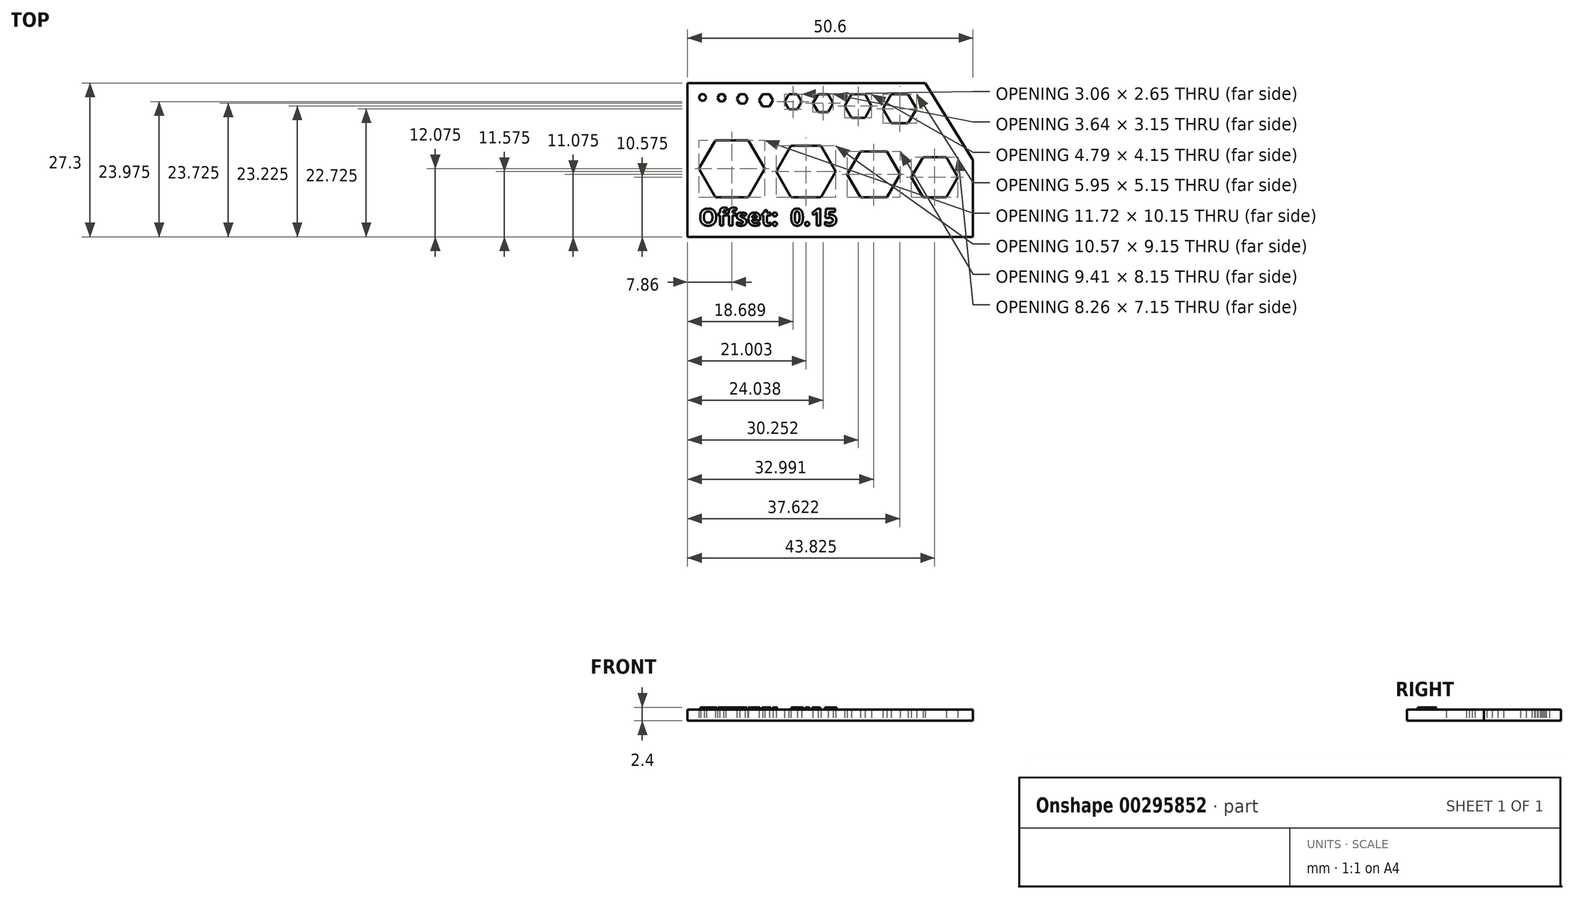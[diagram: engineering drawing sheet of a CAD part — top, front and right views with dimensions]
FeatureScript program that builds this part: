
annotation { "Feature Type Name" : "Feature", "Feature Type Description" : "" }
export const myFeature = defineFeature(function(context is Context, id is Id, definition is map)
    precondition{}
    {
        {
            assignVariable(context, id + "F0", {"variableType" : VariableType.LENGTH, "name" : "HoleOffset", "lengthValue" : 0.15 * mm});
        }
        {
            assignVariable(context, id + "F1", {"variableType" : VariableType.LENGTH, "name" : "HoleDistance", "lengthValue" : 2 * mm});
        }
        {
            assignVariable(context, id + "F2", {"variableType" : VariableType.LENGTH, "name" : "TextHeight", "lengthValue" : 3 * mm});
        }
        {
            assignVariable(context, id + "F3", {"variableType" : VariableType.LENGTH, "name" : "TextRelief", "lengthValue" : 0.4 * mm});
        }
        {
            assignVariable(context, id + "F4", {"variableType" : VariableType.LENGTH, "name" : "BaseWidth", "lengthValue" : 40 * mm + getVariable(context, 'HoleDistance') * 5 + getVariable(context, 'HoleOffset') * 4});
        }
        {
            assignVariable(context, id + "F5", {"variableType" : VariableType.LENGTH, "name" : "BaseHeight", "lengthValue" : 16 * mm + getVariable(context, 'TextHeight') + getVariable(context, 'HoleDistance') * 4 + getVariable(context, 'HoleOffset') * 2});
        }
        {
            assignVariable(context, id + "F6", {"variableType" : VariableType.LENGTH, "name" : "BaseThickness", "lengthValue" : 2 * mm});
        }
        {
            var Q0;
            Q0=qCreatedBy(makeId("Top.planeOp"),FACE);
            var sketch = newSketch(context, id + "F7", { "sketchPlane" : qUnion([Q0])});
            skLineSegment(sketch, "E0.bottom", {"start": v(0, 0) * mm, "end": v(50.6, 0) * mm});
            skLineSegment(sketch, "E0.top", {"start": v(0, -27.3) * mm, "end": v(50.6, -27.3) * mm});
            skLineSegment(sketch, "E0.left", {"start": v(0, 0) * mm, "end": v(0, -27.3) * mm});
            skLineSegment(sketch, "E0.right", {"start": v(50.6, 0) * mm, "end": v(50.6, -27.3) * mm});
            skCircle(sketch, "E1.cCircle", {"center": v(2.66, -2.57) * mm, "radius": 0.57 * mm, "construction": true});
            skLineSegment(sketch, "E1.0", {"start": v(3.33, -2.58) * mm, "end": v(3, -3.15) * mm});
            skLineSegment(sketch, "E1.1", {"start": v(3, -3.15) * mm, "end": v(2.33, -3.15) * mm});
            skLineSegment(sketch, "E1.2", {"start": v(2.33, -3.15) * mm, "end": v(2, -2.57) * mm});
            skLineSegment(sketch, "E1.3", {"start": v(2, -2.57) * mm, "end": v(2.33, -2) * mm});
            skLineSegment(sketch, "E1.4", {"start": v(2.33, -2) * mm, "end": v(3, -2) * mm});
            skLineSegment(sketch, "E1.5", {"start": v(3, -2) * mm, "end": v(3.33, -2.57) * mm});
            skPoint(sketch, "E1.0.midPoint", {"position": v(3.16, -2.86) * mm});
            skCircle(sketch, "E2.cCircle", {"center": v(6.05, -2.62) * mm, "radius": 0.62 * mm, "construction": true});
            skLineSegment(sketch, "E2.0", {"start": v(6.77, -2.63) * mm, "end": v(6.41, -3.25) * mm});
            skLineSegment(sketch, "E2.1", {"start": v(6.41, -3.25) * mm, "end": v(5.69, -3.25) * mm});
            skLineSegment(sketch, "E2.2", {"start": v(5.69, -3.25) * mm, "end": v(5.33, -2.62) * mm});
            skLineSegment(sketch, "E2.3", {"start": v(5.33, -2.62) * mm, "end": v(5.69, -2) * mm});
            skLineSegment(sketch, "E2.4", {"start": v(5.69, -2) * mm, "end": v(6.41, -2) * mm});
            skLineSegment(sketch, "E2.5", {"start": v(6.41, -2) * mm, "end": v(6.77, -2.62) * mm});
            skPoint(sketch, "E2.0.midPoint", {"position": v(6.6, -2.94) * mm});
            skCircle(sketch, "E3.cCircle", {"center": v(9.72, -2.82) * mm, "radius": 0.82 * mm, "construction": true});
            skLineSegment(sketch, "E3.0", {"start": v(10.68, -2.83) * mm, "end": v(10.2, -3.65) * mm});
            skLineSegment(sketch, "E3.1", {"start": v(10.2, -3.65) * mm, "end": v(9.25, -3.65) * mm});
            skLineSegment(sketch, "E3.2", {"start": v(9.25, -3.65) * mm, "end": v(8.77, -2.82) * mm});
            skLineSegment(sketch, "E3.3", {"start": v(8.77, -2.82) * mm, "end": v(9.25, -2) * mm});
            skLineSegment(sketch, "E3.4", {"start": v(9.25, -2) * mm, "end": v(10.2, -2) * mm});
            skLineSegment(sketch, "E3.5", {"start": v(10.2, -2) * mm, "end": v(10.68, -2.83) * mm});
            skPoint(sketch, "E3.0.midPoint", {"position": v(10.44, -3.24) * mm});
            skCircle(sketch, "E4.cCircle", {"center": v(13.92, -3.07) * mm, "radius": 1.07 * mm, "construction": true});
            skLineSegment(sketch, "E4.0", {"start": v(15.16, -3.07) * mm, "end": v(14.54, -4.15) * mm});
            skLineSegment(sketch, "E4.1", {"start": v(14.54, -4.15) * mm, "end": v(13.3, -4.15) * mm});
            skLineSegment(sketch, "E4.2", {"start": v(13.3, -4.15) * mm, "end": v(12.68, -3.07) * mm});
            skLineSegment(sketch, "E4.3", {"start": v(12.68, -3.07) * mm, "end": v(13.3, -2) * mm});
            skLineSegment(sketch, "E4.4", {"start": v(13.3, -2) * mm, "end": v(14.54, -2) * mm});
            skLineSegment(sketch, "E4.5", {"start": v(14.54, -2) * mm, "end": v(15.16, -3.07) * mm});
            skPoint(sketch, "E4.0.midPoint", {"position": v(14.85, -3.61) * mm});
            skCircle(sketch, "E5.cCircle", {"center": v(18.69, -3.32) * mm, "radius": 1.32 * mm, "construction": true});
            skLineSegment(sketch, "E5.0", {"start": v(20.22, -3.33) * mm, "end": v(19.45, -4.65) * mm});
            skLineSegment(sketch, "E5.1", {"start": v(19.45, -4.65) * mm, "end": v(17.92, -4.65) * mm});
            skLineSegment(sketch, "E5.2", {"start": v(17.92, -4.65) * mm, "end": v(17.16, -3.32) * mm});
            skLineSegment(sketch, "E5.3", {"start": v(17.16, -3.32) * mm, "end": v(17.92, -2) * mm});
            skLineSegment(sketch, "E5.4", {"start": v(17.92, -2) * mm, "end": v(19.45, -2) * mm});
            skLineSegment(sketch, "E5.5", {"start": v(19.45, -2) * mm, "end": v(20.22, -3.33) * mm});
            skPoint(sketch, "E5.0.midPoint", {"position": v(19.84, -3.99) * mm});
            skCircle(sketch, "E6.cCircle", {"center": v(24.04, -3.57) * mm, "radius": 1.57 * mm, "construction": true});
            skLineSegment(sketch, "E6.0", {"start": v(25.86, -3.58) * mm, "end": v(24.95, -5.15) * mm});
            skLineSegment(sketch, "E6.1", {"start": v(24.95, -5.15) * mm, "end": v(23.13, -5.15) * mm});
            skLineSegment(sketch, "E6.2", {"start": v(23.13, -5.15) * mm, "end": v(22.22, -3.58) * mm});
            skLineSegment(sketch, "E6.3", {"start": v(22.22, -3.58) * mm, "end": v(23.13, -2) * mm});
            skLineSegment(sketch, "E6.4", {"start": v(23.13, -2) * mm, "end": v(24.95, -2) * mm});
            skLineSegment(sketch, "E6.5", {"start": v(24.95, -2) * mm, "end": v(25.86, -3.57) * mm});
            skPoint(sketch, "E6.0.midPoint", {"position": v(25.4, -4.36) * mm});
            skCircle(sketch, "E7.cCircle", {"center": v(30.25, -4.08) * mm, "radius": 2.08 * mm, "construction": true});
            skLineSegment(sketch, "E7.0", {"start": v(32.65, -4.07) * mm, "end": v(31.45, -6.15) * mm});
            skLineSegment(sketch, "E7.1", {"start": v(31.45, -6.15) * mm, "end": v(29.05, -6.15) * mm});
            skLineSegment(sketch, "E7.2", {"start": v(29.05, -6.15) * mm, "end": v(27.86, -4.08) * mm});
            skLineSegment(sketch, "E7.3", {"start": v(27.86, -4.08) * mm, "end": v(29.05, -2) * mm});
            skLineSegment(sketch, "E7.4", {"start": v(29.05, -2) * mm, "end": v(31.45, -2) * mm});
            skLineSegment(sketch, "E7.5", {"start": v(31.45, -2) * mm, "end": v(32.65, -4.07) * mm});
            skPoint(sketch, "E7.0.midPoint", {"position": v(32.05, -5.11) * mm});
            skCircle(sketch, "E8.cCircle", {"center": v(37.62, -4.58) * mm, "radius": 2.58 * mm, "construction": true});
            skLineSegment(sketch, "E8.0", {"start": v(40.6, -4.58) * mm, "end": v(39.1, -7.15) * mm});
            skLineSegment(sketch, "E8.1", {"start": v(39.1, -7.15) * mm, "end": v(36.14, -7.15) * mm});
            skLineSegment(sketch, "E8.2", {"start": v(36.14, -7.15) * mm, "end": v(34.65, -4.57) * mm});
            skLineSegment(sketch, "E8.3", {"start": v(34.65, -4.58) * mm, "end": v(36.14, -2) * mm});
            skLineSegment(sketch, "E8.4", {"start": v(36.14, -2) * mm, "end": v(39.1, -2) * mm});
            skLineSegment(sketch, "E8.5", {"start": v(39.1, -2) * mm, "end": v(40.6, -4.57) * mm});
            skPoint(sketch, "E8.0.midPoint", {"position": v(39.85, -5.86) * mm});
            skCircle(sketch, "E9.cCircle", {"center": v(7.86, -15.23) * mm, "radius": 5.08 * mm, "construction": true});
            skLineSegment(sketch, "E9.0", {"start": v(13.72, -15.23) * mm, "end": v(10.8, -20.3) * mm});
            skLineSegment(sketch, "E9.1", {"start": v(10.8, -20.3) * mm, "end": v(4.93, -20.3) * mm});
            skLineSegment(sketch, "E9.2", {"start": v(4.93, -20.3) * mm, "end": v(2, -15.23) * mm});
            skLineSegment(sketch, "E9.3", {"start": v(2, -15.22) * mm, "end": v(4.93, -10.15) * mm});
            skLineSegment(sketch, "E9.4", {"start": v(4.93, -10.15) * mm, "end": v(10.8, -10.15) * mm});
            skLineSegment(sketch, "E9.5", {"start": v(10.8, -10.15) * mm, "end": v(13.72, -15.23) * mm});
            skPoint(sketch, "E9.0.midPoint", {"position": v(12.26, -17.76) * mm});
            skCircle(sketch, "E10.cCircle", {"center": v(21, -15.72) * mm, "radius": 4.58 * mm, "construction": true});
            skLineSegment(sketch, "E10.0", {"start": v(26.29, -15.72) * mm, "end": v(23.64, -20.3) * mm});
            skLineSegment(sketch, "E10.1", {"start": v(23.64, -20.3) * mm, "end": v(18.36, -20.3) * mm});
            skLineSegment(sketch, "E10.2", {"start": v(18.36, -20.3) * mm, "end": v(15.72, -15.72) * mm});
            skLineSegment(sketch, "E10.3", {"start": v(15.72, -15.73) * mm, "end": v(18.36, -11.15) * mm});
            skLineSegment(sketch, "E10.4", {"start": v(18.36, -11.15) * mm, "end": v(23.64, -11.15) * mm});
            skLineSegment(sketch, "E10.5", {"start": v(23.64, -11.15) * mm, "end": v(26.29, -15.72) * mm});
            skPoint(sketch, "E10.0.midPoint", {"position": v(24.97, -18.01) * mm});
            skCircle(sketch, "E11.cCircle", {"center": v(33, -16.23) * mm, "radius": 4.08 * mm, "construction": true});
            skLineSegment(sketch, "E11.0", {"start": v(37.7, -16.23) * mm, "end": v(35.34, -20.3) * mm});
            skLineSegment(sketch, "E11.1", {"start": v(35.34, -20.3) * mm, "end": v(30.64, -20.3) * mm});
            skLineSegment(sketch, "E11.2", {"start": v(30.64, -20.3) * mm, "end": v(28.29, -16.22) * mm});
            skLineSegment(sketch, "E11.3", {"start": v(28.29, -16.22) * mm, "end": v(30.64, -12.15) * mm});
            skLineSegment(sketch, "E11.4", {"start": v(30.64, -12.15) * mm, "end": v(35.34, -12.15) * mm});
            skLineSegment(sketch, "E11.5", {"start": v(35.34, -12.15) * mm, "end": v(37.7, -16.23) * mm});
            skPoint(sketch, "E11.0.midPoint", {"position": v(36.52, -18.26) * mm});
            skCircle(sketch, "E12.cCircle", {"center": v(43.82, -16.72) * mm, "radius": 3.58 * mm, "construction": true});
            skLineSegment(sketch, "E12.0", {"start": v(47.95, -16.73) * mm, "end": v(45.89, -20.3) * mm});
            skLineSegment(sketch, "E12.1", {"start": v(45.89, -20.3) * mm, "end": v(41.76, -20.3) * mm});
            skLineSegment(sketch, "E12.2", {"start": v(41.76, -20.3) * mm, "end": v(39.7, -16.72) * mm});
            skLineSegment(sketch, "E12.3", {"start": v(39.7, -16.72) * mm, "end": v(41.76, -13.15) * mm});
            skLineSegment(sketch, "E12.4", {"start": v(41.76, -13.15) * mm, "end": v(45.89, -13.15) * mm});
            skLineSegment(sketch, "E12.5", {"start": v(45.89, -13.15) * mm, "end": v(47.95, -16.72) * mm});
            skPoint(sketch, "E12.0.midPoint", {"position": v(46.92, -18.51) * mm});
            skSolve(sketch);
        }
        {
            var Q0;
            Q0=makeQuery(id+"F7.imprint","IMPRINT",FACE,{"disambiguationData":[TD([[makeQuery(id+"F7.imprint","IMPRINT",EDGE,{"derivedFrom":sQuery(id+"F7.wireOp",EDGE,"E0.bottom")}),-1.0]])]});
            extrude(context, id + "F8", {"entities" : qUnion([Q0]), "depth" : getVariable(context, 'BaseThickness'), "offsetDistance" : 25 * mm});
        }
        {
            var Q0;
            Q0=makeQuery(id+"F8.opExtrude","CAP_FACE",FACE,{"disambiguationData":[OSD([sQuery(id+"F7.wireOp",EDGE,"E0.bottom"),sQuery(id+"F7.wireOp",EDGE,"E0.top"),sQuery(id+"F7.wireOp",EDGE,"E0.left"),sQuery(id+"F7.wireOp",EDGE,"E0.right"),sQuery(id+"F7.wireOp",EDGE,"E1.0"),sQuery(id+"F7.wireOp",EDGE,"E1.1"),sQuery(id+"F7.wireOp",EDGE,"E1.2"),sQuery(id+"F7.wireOp",EDGE,"E1.3"),sQuery(id+"F7.wireOp",EDGE,"E1.4"),sQuery(id+"F7.wireOp",EDGE,"E1.5"),sQuery(id+"F7.wireOp",EDGE,"E2.0"),sQuery(id+"F7.wireOp",EDGE,"E2.1"),sQuery(id+"F7.wireOp",EDGE,"E2.2"),sQuery(id+"F7.wireOp",EDGE,"E2.3"),sQuery(id+"F7.wireOp",EDGE,"E2.4"),sQuery(id+"F7.wireOp",EDGE,"E2.5"),sQuery(id+"F7.wireOp",EDGE,"E3.0"),sQuery(id+"F7.wireOp",EDGE,"E3.1"),sQuery(id+"F7.wireOp",EDGE,"E3.2"),sQuery(id+"F7.wireOp",EDGE,"E3.3"),sQuery(id+"F7.wireOp",EDGE,"E3.4"),sQuery(id+"F7.wireOp",EDGE,"E3.5"),sQuery(id+"F7.wireOp",EDGE,"E4.0"),sQuery(id+"F7.wireOp",EDGE,"E4.1"),sQuery(id+"F7.wireOp",EDGE,"E4.2"),sQuery(id+"F7.wireOp",EDGE,"E4.3"),sQuery(id+"F7.wireOp",EDGE,"E4.4"),sQuery(id+"F7.wireOp",EDGE,"E4.5"),sQuery(id+"F7.wireOp",EDGE,"E5.0"),sQuery(id+"F7.wireOp",EDGE,"E5.1"),sQuery(id+"F7.wireOp",EDGE,"E5.2"),sQuery(id+"F7.wireOp",EDGE,"E5.3"),sQuery(id+"F7.wireOp",EDGE,"E5.4"),sQuery(id+"F7.wireOp",EDGE,"E5.5"),sQuery(id+"F7.wireOp",EDGE,"E6.0"),sQuery(id+"F7.wireOp",EDGE,"E6.1"),sQuery(id+"F7.wireOp",EDGE,"E6.2"),sQuery(id+"F7.wireOp",EDGE,"E6.3"),sQuery(id+"F7.wireOp",EDGE,"E6.4"),sQuery(id+"F7.wireOp",EDGE,"E6.5"),sQuery(id+"F7.wireOp",EDGE,"E7.0"),sQuery(id+"F7.wireOp",EDGE,"E7.1"),sQuery(id+"F7.wireOp",EDGE,"E7.2"),sQuery(id+"F7.wireOp",EDGE,"E7.3"),sQuery(id+"F7.wireOp",EDGE,"E7.4"),sQuery(id+"F7.wireOp",EDGE,"E7.5"),sQuery(id+"F7.wireOp",EDGE,"E8.0"),sQuery(id+"F7.wireOp",EDGE,"E8.1"),sQuery(id+"F7.wireOp",EDGE,"E8.2"),sQuery(id+"F7.wireOp",EDGE,"E8.3"),sQuery(id+"F7.wireOp",EDGE,"E8.4"),sQuery(id+"F7.wireOp",EDGE,"E8.5"),sQuery(id+"F7.wireOp",EDGE,"E9.0"),sQuery(id+"F7.wireOp",EDGE,"E9.1"),sQuery(id+"F7.wireOp",EDGE,"E9.2"),sQuery(id+"F7.wireOp",EDGE,"E9.3"),sQuery(id+"F7.wireOp",EDGE,"E9.4"),sQuery(id+"F7.wireOp",EDGE,"E9.5"),sQuery(id+"F7.wireOp",EDGE,"E10.0"),sQuery(id+"F7.wireOp",EDGE,"E10.1"),sQuery(id+"F7.wireOp",EDGE,"E10.2"),sQuery(id+"F7.wireOp",EDGE,"E10.3"),sQuery(id+"F7.wireOp",EDGE,"E10.4"),sQuery(id+"F7.wireOp",EDGE,"E10.5"),sQuery(id+"F7.wireOp",EDGE,"E11.0"),sQuery(id+"F7.wireOp",EDGE,"E11.1"),sQuery(id+"F7.wireOp",EDGE,"E11.2"),sQuery(id+"F7.wireOp",EDGE,"E11.3"),sQuery(id+"F7.wireOp",EDGE,"E11.4"),sQuery(id+"F7.wireOp",EDGE,"E11.5"),sQuery(id+"F7.wireOp",EDGE,"E12.0"),sQuery(id+"F7.wireOp",EDGE,"E12.1"),sQuery(id+"F7.wireOp",EDGE,"E12.2"),sQuery(id+"F7.wireOp",EDGE,"E12.3"),sQuery(id+"F7.wireOp",EDGE,"E12.4"),sQuery(id+"F7.wireOp",EDGE,"E12.5")])],"isStart":false});
            cPlane(context, id + "F9", {"entities" : qUnion([Q0]), "cplaneType" : CPlaneType.OFFSET, "offset" : 0 * mm, "width" : 150 * mm, "height" : 150 * mm});
        }
        {
            var Q0;
            Q0=qCreatedBy(id+"F9.planeOp",FACE);
            var sketch = newSketch(context, id + "F10", { "sketchPlane" : qUnion([Q0])});
            skText(sketch, "E13", { "text": "Offset:  0.15", "fontName": "OpenSans-Bold.ttf"});
            const initialGuessF10  = {"E13": [0.002, -0.0253, 1, 0, 0.003]};
            skSetInitialGuess(sketch, initialGuessF10);
            skSolve(sketch);
        }
        {
            var Q0;
            Q0 = qSketchRegion(id + "F10", true);
            extrude(context, id + "F11", {"entities" : qUnion([Q0]), "operationType" : NewBodyOperationType.ADD, "depth" : getVariable(context, 'TextRelief'), "offsetDistance" : 25 * mm});
        }
        {
            var Q0;
            Q0=makeQuery(id+"F8.opExtrude","SWEPT_EDGE",EDGE,{"disambiguationData":[OSD([sQuery(id+"F7.wireOp",EDGE,"E0.bottom"),sQuery(id+"F7.wireOp",EDGE,"E0.right")])]});
            chamfer(context, id + "F12", {"entities" : qUnion([Q0]), "chamferType" : ChamferType.TWO_OFFSETS, "width1" : getVariable(context, 'BaseWidth') / 6, "oppositeDirection" : false, "width2" : getVariable(context, 'BaseHeight') / 2, "tangentPropagation" : true});
        }
    });
